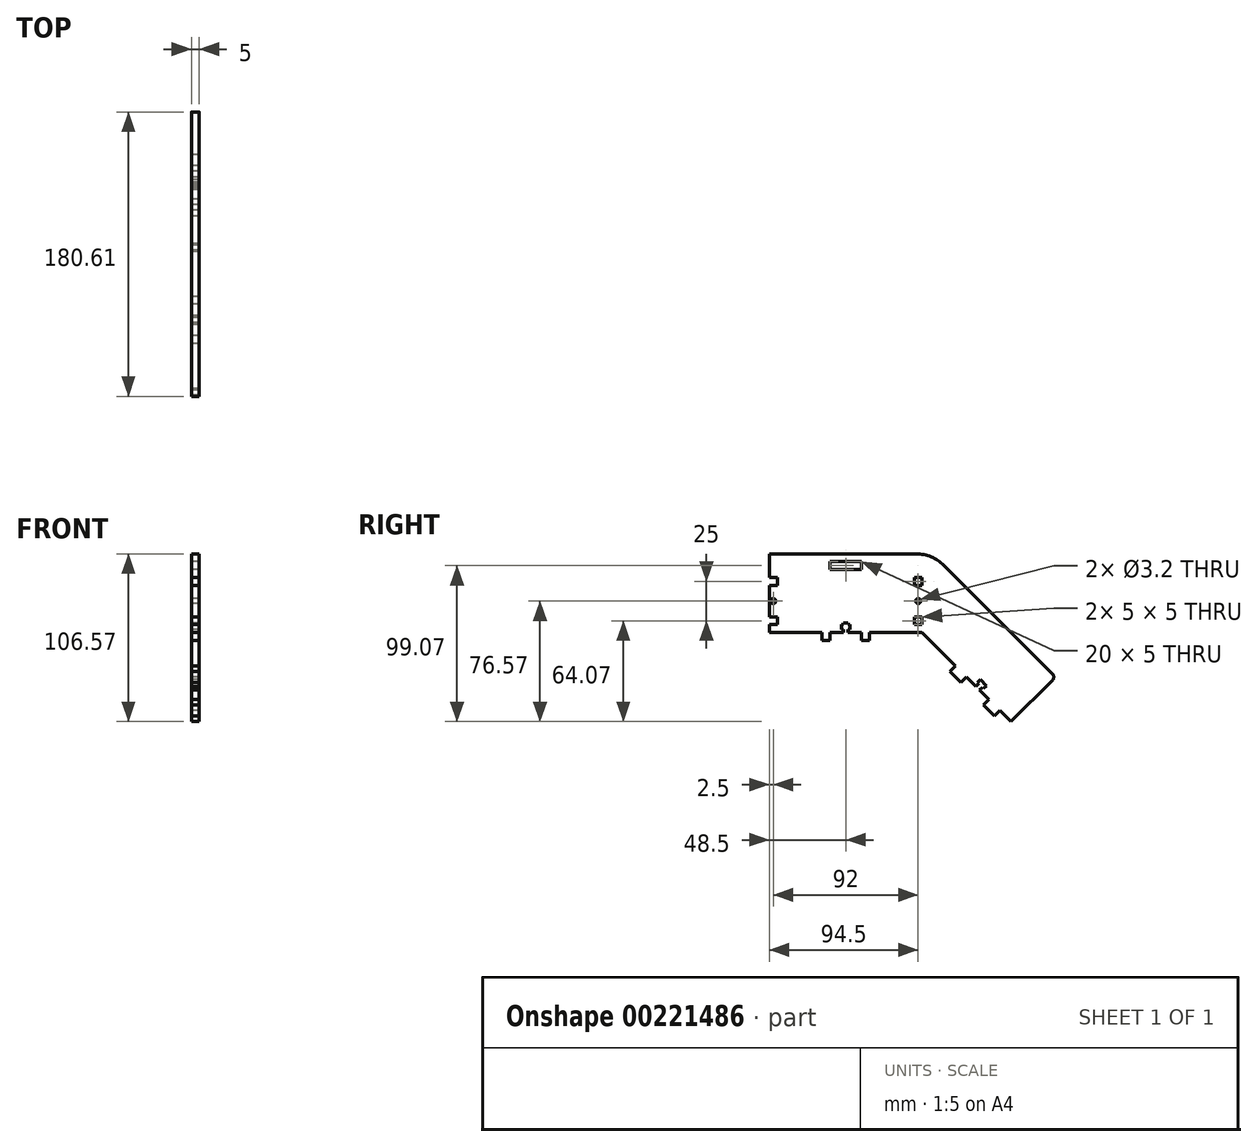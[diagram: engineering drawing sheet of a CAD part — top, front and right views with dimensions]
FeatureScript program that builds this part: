
annotation { "Feature Type Name" : "Feature", "Feature Type Description" : "" }
export const myFeature = defineFeature(function(context is Context, id is Id, definition is map)
    precondition{}
    {
        {
            assignVariable(context, id + "F0", {"name" : "thickness", "anyValue" : 5 * mm});
        }
        {
            var Q0;
            Q0=qCreatedBy(makeId("Right.planeOp"),FACE);
            var sketch = newSketch(context, id + "F1", { "sketchPlane" : qUnion([Q0])});
            skLineSegment(sketch, "E0.bottom", {"start": v(0, 0) * mm, "end": v(33.5, 0) * mm});
            skLineSegment(sketch, "E0.top", {"start": v(0, 40) * mm, "end": v(33.5, 40) * mm, "construction": true});
            skLineSegment(sketch, "E0.left", {"start": v(0, 0) * mm, "end": v(0, 5) * mm});
            skLineSegment(sketch, "E1", {"start": v(33.5, 40) * mm, "end": v(33.5, 45) * mm, "construction": true});
            skLineSegment(sketch, "E2", {"start": v(33.5, 45) * mm, "end": v(38.5, 45) * mm, "construction": true});
            skLineSegment(sketch, "E3", {"start": v(38.5, 45) * mm, "end": v(38.5, 40) * mm});
            skLineSegment(sketch, "E4", {"start": v(58.5, 40) * mm, "end": v(58.5, 45) * mm});
            skLineSegment(sketch, "E5", {"start": v(58.5, 45) * mm, "end": v(63.5, 45) * mm, "construction": true});
            skLineSegment(sketch, "E6", {"start": v(63.5, 45) * mm, "end": v(63.5, 40) * mm, "construction": true});
            skLineSegment(sketch, "E7", {"start": v(0, 20) * mm, "end": v(105.28, 20) * mm, "construction": true});
            skLineSegment(sketch, "E8", {"start": v(48.5, 40) * mm, "end": v(48.5, 0) * mm, "construction": true});
            skLineSegment(sketch, "E9", {"start": v(47, 40) * mm, "end": v(47, 38) * mm, "construction": true});
            skLineSegment(sketch, "E10", {"start": v(47, 38) * mm, "end": v(45.75, 38) * mm, "construction": true});
            skLineSegment(sketch, "E11", {"start": v(45.75, 38) * mm, "end": v(45.75, 35) * mm, "construction": true});
            skLineSegment(sketch, "E12", {"start": v(45.75, 35) * mm, "end": v(47, 35) * mm, "construction": true});
            skLineSegment(sketch, "E13", {"start": v(47, 35) * mm, "end": v(47, 34) * mm, "construction": true});
            skLineSegment(sketch, "E14", {"start": v(47, 34) * mm, "end": v(50, 34) * mm, "construction": true});
            skLineSegment(sketch, "E15", {"start": v(50, 34) * mm, "end": v(50, 35) * mm, "construction": true});
            skLineSegment(sketch, "E16", {"start": v(50, 35) * mm, "end": v(51.25, 35) * mm, "construction": true});
            skLineSegment(sketch, "E17", {"start": v(51.25, 35) * mm, "end": v(51.25, 38) * mm, "construction": true});
            skLineSegment(sketch, "E18", {"start": v(51.25, 38) * mm, "end": v(50, 38) * mm, "construction": true});
            skLineSegment(sketch, "E19", {"start": v(50, 38) * mm, "end": v(50, 40) * mm, "construction": true});
            skPoint(sketch, "E20", {"position": v(48.5, 34) * mm});
            skLineSegment(sketch, "E21.trimOffspring", {"start": v(50, 40) * mm, "end": v(58.5, 40) * mm, "construction": true});
            skLineSegment(sketch, "E22.trimOffspring", {"start": v(38.5, 40) * mm, "end": v(47, 40) * mm, "construction": true});
            skCircle(sketch, "E23", {"center": v(2.5, 20) * mm, "radius": 1.6 * mm});
            skLineSegment(sketch, "E24", {"start": v(0, 35) * mm, "end": v(5, 35) * mm});
            skLineSegment(sketch, "E25", {"start": v(5, 35) * mm, "end": v(5, 30) * mm});
            skLineSegment(sketch, "E26", {"start": v(5, 30) * mm, "end": v(0, 30) * mm});
            skLineSegment(sketch, "E27", {"start": v(0, 10) * mm, "end": v(5, 10) * mm});
            skLineSegment(sketch, "E28", {"start": v(5, 10) * mm, "end": v(5, 5) * mm});
            skLineSegment(sketch, "E29", {"start": v(5, 5) * mm, "end": v(0, 5) * mm});
            skPoint(sketch, "E30", {"position": v(2.5, 30) * mm});
            skLineSegment(sketch, "E31.trimOffspring", {"start": v(0, 35) * mm, "end": v(0, 40) * mm});
            skLineSegment(sketch, "E32.trimOffspring", {"start": v(0, 10) * mm, "end": v(0, 30) * mm});
            skLineSegment(sketch, "E33.trimOffspring", {"start": v(50, 0) * mm, "end": v(58.5, 0) * mm});
            skLineSegment(sketch, "E34.MirrorCS", {"start": v(51.25, 2) * mm, "end": v(50, 2) * mm});
            skLineSegment(sketch, "E35.MirrorCS", {"start": v(50, 6) * mm, "end": v(50, 5) * mm});
            skLineSegment(sketch, "E36.MirrorCS", {"start": v(50, 2) * mm, "end": v(50, 0) * mm});
            skLineSegment(sketch, "E37.MirrorCS", {"start": v(45.75, 5) * mm, "end": v(47, 5) * mm});
            skLineSegment(sketch, "E38.MirrorCS", {"start": v(47, 2) * mm, "end": v(45.75, 2) * mm});
            skLineSegment(sketch, "E39.MirrorCS", {"start": v(50, 5) * mm, "end": v(51.25, 5) * mm});
            skLineSegment(sketch, "E40.MirrorCS", {"start": v(47, 5) * mm, "end": v(47, 6) * mm});
            skLineSegment(sketch, "E41.MirrorCS", {"start": v(47, 0) * mm, "end": v(47, 2) * mm});
            skLineSegment(sketch, "E42.MirrorCS", {"start": v(47, 6) * mm, "end": v(50, 6) * mm});
            skLineSegment(sketch, "E43.MirrorCS", {"start": v(38.5, 0) * mm, "end": v(47, 0) * mm});
            skLineSegment(sketch, "E44.MirrorCS", {"start": v(51.25, 5) * mm, "end": v(51.25, 2) * mm});
            skLineSegment(sketch, "E45.MirrorCS", {"start": v(58.5, -5) * mm, "end": v(63.5, -5) * mm});
            skLineSegment(sketch, "E46.MirrorCS", {"start": v(58.5, 0) * mm, "end": v(58.5, -5) * mm});
            skLineSegment(sketch, "E47.MirrorCS", {"start": v(33.5, 0) * mm, "end": v(33.5, -5) * mm});
            skLineSegment(sketch, "E48.MirrorCS", {"start": v(45.75, 2) * mm, "end": v(45.75, 5) * mm});
            skPoint(sketch, "E49.MirrorP", {"position": v(48.5, 6) * mm});
            skLineSegment(sketch, "E50.MirrorCS", {"start": v(63.5, -5) * mm, "end": v(63.5, 0) * mm});
            skLineSegment(sketch, "E51.MirrorCS", {"start": v(38.5, -5) * mm, "end": v(38.5, 0) * mm});
            skLineSegment(sketch, "E52.MirrorCS", {"start": v(33.5, -5) * mm, "end": v(38.5, -5) * mm});
            skLineSegment(sketch, "E53.trimOffspring", {"start": v(63.5, 0) * mm, "end": v(97, 0) * mm});
            skLineSegment(sketch, "E54", {"start": v(97, 0) * mm, "end": v(131.22, -34.22) * mm});
            skLineSegment(sketch, "E55", {"start": v(153.57, -56.57) * mm, "end": v(179.73, -30.4) * mm});
            skLineSegment(sketch, "E56", {"start": v(179.73, -26.16) * mm, "end": v(110.9, 42.68) * mm});
            skLineSegment(sketch, "E57", {"start": v(63.5, 40) * mm, "end": v(103.57, 40) * mm, "construction": true});
            skLineSegment(sketch, "E58", {"start": v(97, 0) * mm, "end": v(113.57, 40) * mm, "construction": true});
            skLineSegment(sketch, "E59", {"start": v(146.5, -49.5) * mm, "end": v(142.96, -53.03) * mm});
            skLineSegment(sketch, "E60", {"start": v(142.96, -53.03) * mm, "end": v(135.9, -45.96) * mm});
            skLineSegment(sketch, "E61", {"start": v(135.9, -45.96) * mm, "end": v(139.43, -42.43) * mm});
            skLineSegment(sketch, "E62", {"start": v(125.28, -28.28) * mm, "end": v(121.75, -31.82) * mm});
            skLineSegment(sketch, "E63", {"start": v(121.75, -31.82) * mm, "end": v(114.68, -24.75) * mm});
            skLineSegment(sketch, "E64", {"start": v(114.68, -24.75) * mm, "end": v(118.21, -21.21) * mm});
            skLineSegment(sketch, "E65", {"start": v(132.36, -35.36) * mm, "end": v(160.64, -7.07) * mm, "construction": true});
            skLineSegment(sketch, "E66", {"start": v(131.22, -34.22) * mm, "end": v(133, -32.46) * mm});
            skLineSegment(sketch, "E67", {"start": v(133, -32.46) * mm, "end": v(132.18, -31.64) * mm});
            skLineSegment(sketch, "E68", {"start": v(132.18, -31.64) * mm, "end": v(133.95, -29.88) * mm});
            skLineSegment(sketch, "E69", {"start": v(133.95, -29.88) * mm, "end": v(135.9, -31.82) * mm});
            skLineSegment(sketch, "E70.MirrorCS", {"start": v(133.49, -36.49) * mm, "end": v(135.25, -34.72) * mm});
            skLineSegment(sketch, "E71.MirrorCS", {"start": v(135.25, -34.72) * mm, "end": v(136.07, -35.53) * mm});
            skLineSegment(sketch, "E72.MirrorCS", {"start": v(136.07, -35.53) * mm, "end": v(137.84, -33.76) * mm});
            skLineSegment(sketch, "E73.MirrorCS", {"start": v(137.84, -33.76) * mm, "end": v(135.9, -31.82) * mm});
            skLineSegment(sketch, "E74.trimOffspring", {"start": v(133.49, -36.49) * mm, "end": v(153.57, -56.57) * mm});
            skPoint(sketch, "E75.visualSharp", {"position": v(113.57, 40) * mm});
            skPoint(sketch, "E76.visualSharp", {"position": v(181.85, -28.28) * mm});
            skArc(sketch, "E76.filletArc", {"start": v(179.73, -30.4) * mm, "mid": v(180.61, -28.28) * mm, "end": v(179.73, -26.16) * mm});
            skLineSegment(sketch, "E77", {"start": v(0, 40) * mm, "end": v(0, 50) * mm});
            skLineSegment(sketch, "E78", {"start": v(0, 50) * mm, "end": v(93.21, 50) * mm});
            skLineSegment(sketch, "E79", {"start": v(38.5, 45) * mm, "end": v(58.5, 45) * mm});
            skLineSegment(sketch, "E80", {"start": v(38.5, 40) * mm, "end": v(58.5, 40) * mm});
            skLineSegment(sketch, "E81", {"start": v(97, 0) * mm, "end": v(97, 40) * mm, "construction": true});
            skPoint(sketch, "E82.visualSharp", {"position": v(103.57, 50) * mm});
            skArc(sketch, "E82.filletArc", {"start": v(110.9, 42.68) * mm, "mid": v(102.78, 48.1) * mm, "end": v(93.21, 50) * mm});
            skLineSegment(sketch, "E83.bottom", {"start": v(97, 5) * mm, "end": v(92, 5) * mm});
            skLineSegment(sketch, "E83.top", {"start": v(97, 10) * mm, "end": v(92, 10) * mm});
            skLineSegment(sketch, "E83.left", {"start": v(97, 5) * mm, "end": v(97, 10) * mm});
            skLineSegment(sketch, "E83.right", {"start": v(92, 5) * mm, "end": v(92, 10) * mm});
            skCircle(sketch, "E84", {"center": v(94.5, 20) * mm, "radius": 1.6 * mm});
            skPoint(sketch, "E84.centerSnap0", {"position": v(94.5, 10) * mm});
            skPoint(sketch, "E85.MirrorP", {"position": v(94.5, 30) * mm});
            skLineSegment(sketch, "E86.MirrorCS", {"start": v(92, 35) * mm, "end": v(92, 30) * mm});
            skLineSegment(sketch, "E87.MirrorCS", {"start": v(97, 30) * mm, "end": v(92, 30) * mm});
            skLineSegment(sketch, "E88.MirrorCS", {"start": v(97, 35) * mm, "end": v(97, 30) * mm});
            skLineSegment(sketch, "E89.MirrorCS", {"start": v(97, 35) * mm, "end": v(92, 35) * mm});
            skSolve(sketch);
        }
        {
            var Q0;
            Q0 = qSketchRegion(id + "F1", true);
            extrude(context, id + "F2", {"entities" : qUnion([Q0]), "depth" : getVariable(context, 'thickness')});
        }
    });
